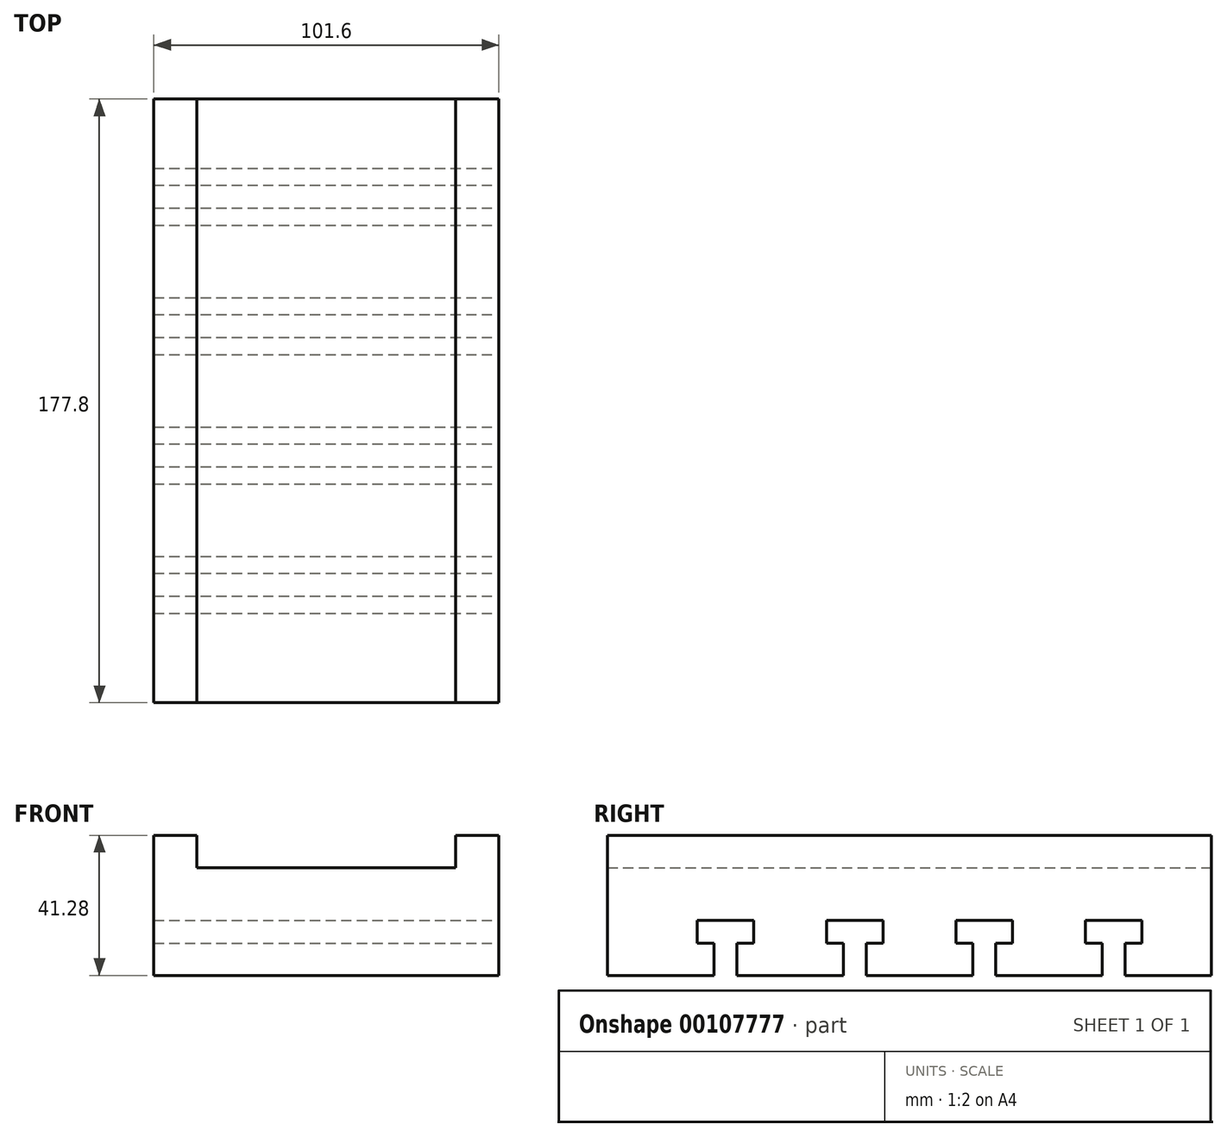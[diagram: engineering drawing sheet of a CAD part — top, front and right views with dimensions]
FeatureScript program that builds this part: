
annotation { "Feature Type Name" : "Feature", "Feature Type Description" : "" }
export const myFeature = defineFeature(function(context is Context, id is Id, definition is map)
    precondition{}
    {
        {
            var Q0;
            Q0=qCreatedBy(makeId("Top.planeOp"),FACE);
            var sketch = newSketch(context, id + "F0", { "sketchPlane" : qUnion([Q0])});
            skLineSegment(sketch, "E0.bottom", {"start": v(-60.1, 0) * mm, "end": v(41.5, 0) * mm});
            skLineSegment(sketch, "E0.top", {"start": v(-60.1, -177.8) * mm, "end": v(41.5, -177.8) * mm});
            skLineSegment(sketch, "E0.left", {"start": v(-60.1, 0) * mm, "end": v(-60.1, -177.8) * mm});
            skLineSegment(sketch, "E0.right", {"start": v(41.5, 0) * mm, "end": v(41.5, -177.8) * mm});
            skSolve(sketch);
        }
        {
            var Q0;
            Q0=makeQuery(id+"F0.imprint","IMPRINT",FACE,{"disambiguationData":[TD([[makeQuery(id+"F0.imprint","IMPRINT",EDGE,{"derivedFrom":sQuery(id+"F0.wireOp",EDGE,"E0.bottom")}),-1.0]])]});
            extrude(context, id + "F1", {"entities" : qUnion([Q0]), "depth" : 15.88 * mm});
        }
        {
            var Q0;
            Q0=makeQuery(id+"F1.opExtrude","CAP_FACE",FACE,{"disambiguationData":[OSD([sQuery(id+"F0.wireOp",EDGE,"E0.bottom"),sQuery(id+"F0.wireOp",EDGE,"E0.top"),sQuery(id+"F0.wireOp",EDGE,"E0.left"),sQuery(id+"F0.wireOp",EDGE,"E0.right")])],"isStart":true});
            extrude(context, id + "F2", {"entities" : qUnion([Q0]), "operationType" : NewBodyOperationType.ADD, "depth" : 15.88 * mm});
        }
        {
            var Q0;
            {var subQ0=sQuery(id+"F0.wireOp",EDGE,"E0.right");Q0=makeQuery(id+"F2.boolean.opBoolean","MERGE",FACE,{"derivedFrom":[makeQuery(id+"F1.opExtrude","SWEPT_FACE",FACE,{"disambiguationData":[OSD([subQ0])]}),makeQuery(id+"F2.opExtrude","SWEPT_FACE",FACE,{"disambiguationData":[OSD([subQ0])]})]});}
            var sketch = newSketch(context, id + "F3", { "sketchPlane" : qUnion([Q0])});
            skLineSegment(sketch, "E1", {"start": v(0, -15.88) * mm, "end": v(-25.4, -15.88) * mm});
            skLineSegment(sketch, "E2", {"start": v(-25.4, -15.88) * mm, "end": v(-25.4, -6.35) * mm});
            skLineSegment(sketch, "E3", {"start": v(-25.4, -6.35) * mm, "end": v(-20.43, -6.35) * mm});
            skLineSegment(sketch, "E4", {"start": v(-20.43, -6.35) * mm, "end": v(-20.43, 0.38) * mm});
            skLineSegment(sketch, "E5", {"start": v(-20.43, 0.38) * mm, "end": v(-37.1, 0.38) * mm});
            skLineSegment(sketch, "E6", {"start": v(-37.1, 0.38) * mm, "end": v(-37.1, -6.35) * mm});
            skLineSegment(sketch, "E7", {"start": v(-37.1, -6.35) * mm, "end": v(-32.12, -6.35) * mm});
            skLineSegment(sketch, "E8", {"start": v(-32.12, -6.35) * mm, "end": v(-32.12, -15.88) * mm});
            skLineSegment(sketch, "E9.1.0.0", {"start": v(-63.5, -15.88) * mm, "end": v(-63.5, -6.35) * mm});
            skLineSegment(sketch, "E9.1.0.1", {"start": v(-63.5, -6.35) * mm, "end": v(-58.53, -6.35) * mm});
            skLineSegment(sketch, "E9.1.0.2", {"start": v(-58.53, -6.35) * mm, "end": v(-58.53, 0.38) * mm});
            skLineSegment(sketch, "E9.1.0.3", {"start": v(-58.53, 0.38) * mm, "end": v(-75.2, 0.38) * mm});
            skLineSegment(sketch, "E9.1.0.4", {"start": v(-75.2, 0.38) * mm, "end": v(-75.2, -6.35) * mm});
            skLineSegment(sketch, "E9.1.0.5", {"start": v(-75.2, -6.35) * mm, "end": v(-70.22, -6.35) * mm});
            skLineSegment(sketch, "E9.1.0.6", {"start": v(-70.22, -6.35) * mm, "end": v(-70.22, -15.88) * mm});
            skLineSegment(sketch, "E9.2.0.0", {"start": v(-101.6, -15.88) * mm, "end": v(-101.6, -6.35) * mm});
            skLineSegment(sketch, "E9.2.0.1", {"start": v(-101.6, -6.35) * mm, "end": v(-96.63, -6.35) * mm});
            skLineSegment(sketch, "E9.2.0.2", {"start": v(-96.63, -6.35) * mm, "end": v(-96.63, 0.38) * mm});
            skLineSegment(sketch, "E9.2.0.3", {"start": v(-96.63, 0.38) * mm, "end": v(-113.3, 0.38) * mm});
            skLineSegment(sketch, "E9.2.0.4", {"start": v(-113.3, 0.38) * mm, "end": v(-113.3, -6.35) * mm});
            skLineSegment(sketch, "E9.2.0.5", {"start": v(-113.3, -6.35) * mm, "end": v(-108.32, -6.35) * mm});
            skLineSegment(sketch, "E9.2.0.6", {"start": v(-108.32, -6.35) * mm, "end": v(-108.32, -15.88) * mm});
            skLineSegment(sketch, "E9.3.0.0", {"start": v(-139.7, -15.88) * mm, "end": v(-139.7, -6.35) * mm});
            skLineSegment(sketch, "E9.3.0.1", {"start": v(-139.7, -6.35) * mm, "end": v(-134.73, -6.35) * mm});
            skLineSegment(sketch, "E9.3.0.2", {"start": v(-134.73, -6.35) * mm, "end": v(-134.73, 0.38) * mm});
            skLineSegment(sketch, "E9.3.0.3", {"start": v(-134.73, 0.38) * mm, "end": v(-151.4, 0.38) * mm});
            skLineSegment(sketch, "E9.3.0.4", {"start": v(-151.4, 0.38) * mm, "end": v(-151.4, -6.35) * mm});
            skLineSegment(sketch, "E9.3.0.5", {"start": v(-151.4, -6.35) * mm, "end": v(-146.42, -6.35) * mm});
            skLineSegment(sketch, "E9.3.0.6", {"start": v(-146.42, -6.35) * mm, "end": v(-146.42, -15.88) * mm});
            skLineSegment(sketch, "E9.direction1", {"start": v(-32.12, -15.88) * mm, "end": v(-70.22, -15.88) * mm, "construction": true});
            skSolve(sketch);
        }
        {
            var Q0;
            {var subQ0=sQuery(id+"F3.wireOp",EDGE,"E2");Q0=makeQuery(id+"F3.imprint","IMPRINT",FACE,{"disambiguationData":[TD([[makeQuery(id+"F3.imprint","IMPRINT",EDGE,{"derivedFrom":subQ0}),1.0]])]});}
            var Q1;
            {var subQ0=sQuery(id+"F3.wireOp",EDGE,"E9.1.0.0");Q1=makeQuery(id+"F3.imprint","IMPRINT",FACE,{"disambiguationData":[TD([[makeQuery(id+"F3.imprint","IMPRINT",EDGE,{"derivedFrom":subQ0}),1.0]])]});}
            var Q2;
            {var subQ0=sQuery(id+"F3.wireOp",EDGE,"E9.2.0.0");Q2=makeQuery(id+"F3.imprint","IMPRINT",FACE,{"disambiguationData":[TD([[makeQuery(id+"F3.imprint","IMPRINT",EDGE,{"derivedFrom":subQ0}),1.0]])]});}
            var Q3;
            {var subQ0=sQuery(id+"F3.wireOp",EDGE,"E9.3.0.0");Q3=makeQuery(id+"F3.imprint","IMPRINT",FACE,{"disambiguationData":[TD([[makeQuery(id+"F3.imprint","IMPRINT",EDGE,{"derivedFrom":subQ0}),1.0]])]});}
            extrude(context, id + "F4", {"entities" : qUnion([Q0, Q1, Q2, Q3]), "operationType" : NewBodyOperationType.REMOVE, "endBound" : BoundingType.THROUGH_ALL, "oppositeDirection" : true, "depth" : 25.4 * mm});
        }
        {
            var Q0;
            Q0=makeQuery(id+"F1.opExtrude","CAP_FACE",FACE,{"disambiguationData":[OSD([sQuery(id+"F0.wireOp",EDGE,"E0.bottom"),sQuery(id+"F0.wireOp",EDGE,"E0.top"),sQuery(id+"F0.wireOp",EDGE,"E0.left"),sQuery(id+"F0.wireOp",EDGE,"E0.right")])],"isStart":false});
            var sketch = newSketch(context, id + "F5", { "sketchPlane" : qUnion([Q0])});
            skLineSegment(sketch, "E10", {"start": v(-60.1, -177.8) * mm, "end": v(-47.4, -177.8) * mm});
            skLineSegment(sketch, "E11", {"start": v(-47.4, -177.8) * mm, "end": v(-47.4, 0) * mm});
            skLineSegment(sketch, "E12", {"start": v(41.5, -177.8) * mm, "end": v(28.8, -177.8) * mm});
            skLineSegment(sketch, "E13", {"start": v(28.8, -177.8) * mm, "end": v(28.8, 0) * mm});
            skSolve(sketch);
        }
        {
            var Q0;
            Q0=makeQuery(id+"F5.imprint","IMPRINT",FACE,{"disambiguationData":[TD([[makeQuery(id+"F5.imprint","IMPRINT",EDGE,{"derivedFrom":sQuery(id+"F5.wireOp",EDGE,"E10")}),1.0]])]});
            var Q1;
            Q1=makeQuery(id+"F5.imprint","IMPRINT",FACE,{"disambiguationData":[TD([[makeQuery(id+"F5.imprint","IMPRINT",EDGE,{"derivedFrom":sQuery(id+"F5.wireOp",EDGE,"E12")}),1.0]])]});
            extrude(context, id + "F6", {"entities" : qUnion([Q0, Q1]), "operationType" : NewBodyOperationType.ADD, "depth" : 9.52 * mm});
        }
    });
